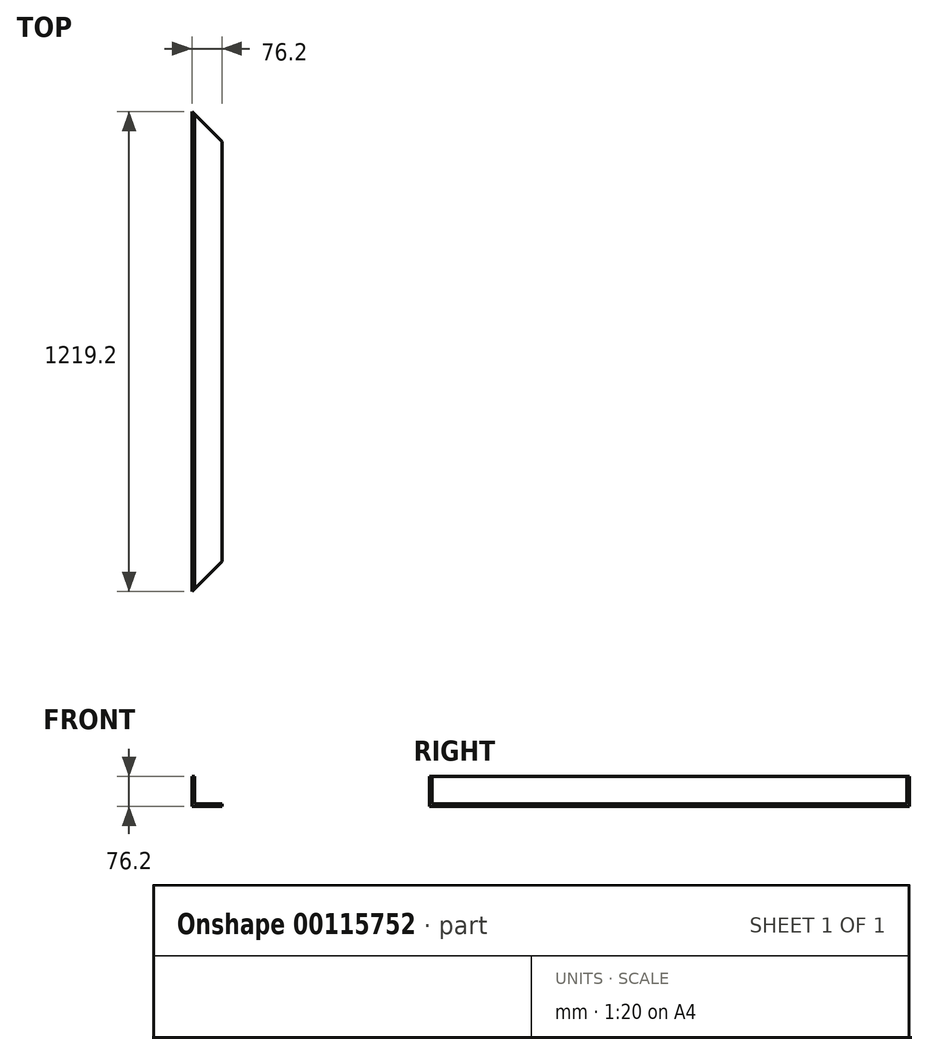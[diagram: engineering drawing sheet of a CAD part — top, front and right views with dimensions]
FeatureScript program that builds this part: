
annotation { "Feature Type Name" : "Feature", "Feature Type Description" : "" }
export const myFeature = defineFeature(function(context is Context, id is Id, definition is map)
    precondition{}
    {
        {
            var Q0;
            Q0=qCreatedBy(makeId("Right.planeOp"),FACE);
            var sketch = newSketch(context, id + "F0", { "sketchPlane" : qUnion([Q0])});
            skLineSegment(sketch, "E0", {"start": v(0, 0) * mm, "end": v(-1219.2, 0) * mm});
            skLineSegment(sketch, "E1.0", {"start": v(0, 76.2) * mm, "end": v(-1219.2, 76.2) * mm});
            skLineSegment(sketch, "E2", {"start": v(-1219.2, 76.2) * mm, "end": v(-1219.2, 0) * mm});
            skLineSegment(sketch, "E3", {"start": v(0, 76.2) * mm, "end": v(0, 0) * mm});
            skSolve(sketch);
        }
        {
            var Q0;
            Q0 = qSketchRegion(id + "F0", true);
            extrude(context, id + "F1", {"entities" : qUnion([Q0]), "oppositeDirection" : true, "depth" : 76.2 * mm});
        }
        {
            var Q0;
            Q0=makeQuery(id+"F1.opExtrude","SWEPT_FACE",FACE,{"disambiguationData":[OSD([sQuery(id+"F0.wireOp",EDGE,"E1.0")])]});
            var sketch = newSketch(context, id + "F2", { "sketchPlane" : qUnion([Q0])});
            skLineSegment(sketch, "E4.0", {"start": v(0, 0) * mm, "end": v(0, -1219.2) * mm});
            skLineSegment(sketch, "E5.0", {"start": v(-69.85, 0) * mm, "end": v(-69.85, -1219.2) * mm});
            skLineSegment(sketch, "E6", {"start": v(-69.85, -1219.2) * mm, "end": v(0, -1219.2) * mm});
            skLineSegment(sketch, "E7", {"start": v(-69.85, 0) * mm, "end": v(0, 0) * mm});
            skSolve(sketch);
        }
        {
            var Q0;
            Q0 = qSketchRegion(id + "F2", true);
            extrude(context, id + "F3", {"entities" : qUnion([Q0]), "operationType" : NewBodyOperationType.REMOVE, "oppositeDirection" : true, "depth" : 69.85 * mm});
        }
        {
            var Q0;
            Q0=makeQuery(id+"F1.opExtrude","SWEPT_FACE",FACE,{"disambiguationData":[OSD([sQuery(id+"F0.wireOp",EDGE,"E1.0")])]});
            var sketch = newSketch(context, id + "F4", { "sketchPlane" : qUnion([Q0])});
            skLineSegment(sketch, "E8.1", {"start": v(0, 0) * mm, "end": v(0, -76.2) * mm});
            skLineSegment(sketch, "E9", {"start": v(-76.2, -1219.2) * mm, "end": v(0, -1143) * mm});
            skLineSegment(sketch, "E10", {"start": v(0, -76.2) * mm, "end": v(-76.2, 0) * mm});
            skLineSegment(sketch, "E11.trimOffspring", {"start": v(0, -1143) * mm, "end": v(0, -1219.2) * mm});
            skLineSegment(sketch, "E12", {"start": v(0, -1219.2) * mm, "end": v(-76.2, -1219.2) * mm});
            skLineSegment(sketch, "E13", {"start": v(0, 0) * mm, "end": v(-76.2, 0) * mm});
            skSolve(sketch);
        }
        {
            var Q0;
            Q0 = qSketchRegion(id + "F4", true);
            extrude(context, id + "F5", {"entities" : qUnion([Q0]), "operationType" : NewBodyOperationType.REMOVE, "oppositeDirection" : true, "depth" : 76.2 * mm});
        }
    });
